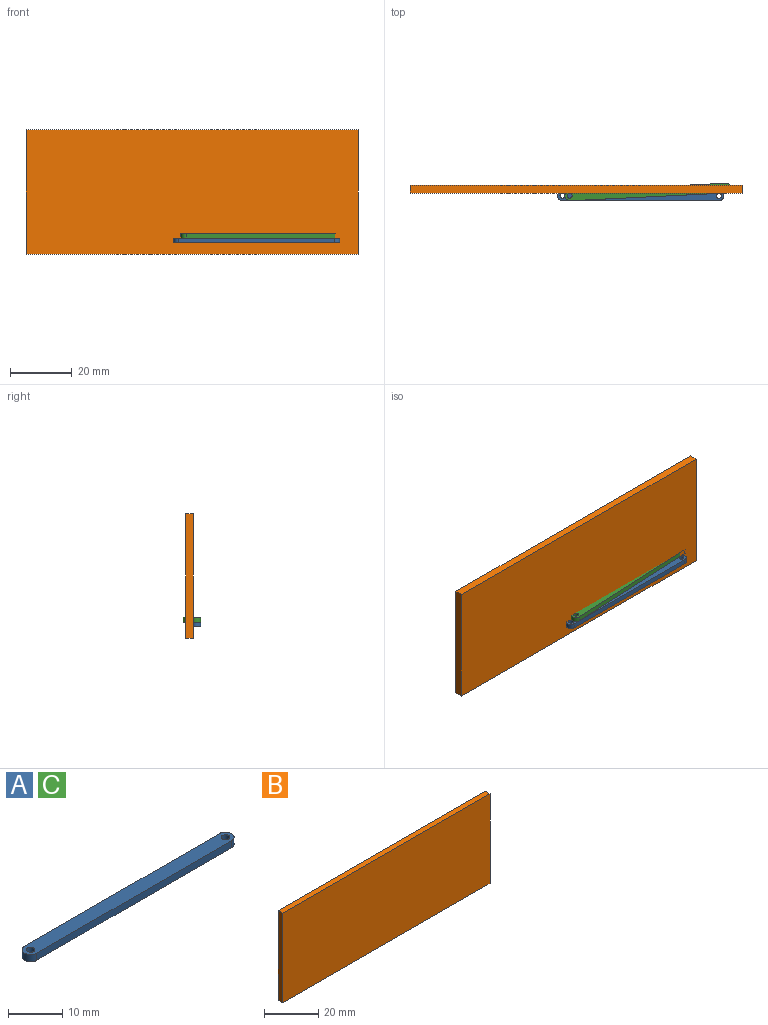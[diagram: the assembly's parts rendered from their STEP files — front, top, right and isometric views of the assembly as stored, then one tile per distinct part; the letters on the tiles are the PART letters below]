
ASSEMBLY  parts=3 mates=2
PART A: 8 faces, bbox 54x3.2x1.6 mm
  f0: plane 50.8x1.59mm, normal (0,1,0), area 80.6mm2, adj f1,f5,f6,f7
  f1: cylinder r=1.59mm len=3.18mm, axis (0,0,-1), area 7.9mm2, adj f0,f2,f6,f7
  f2: plane 50.8x1.59mm, normal (0,-1,0), area 80.6mm2, adj f1,f5,f6,f7
  f3: cylinder r=0.79mm len=1.59mm, axis (0,0,-1), area 7.9mm2, adj f6,f7
  f4: cylinder r=0.79mm len=1.59mm, axis (0,0,-1), area 7.9mm2, adj f6,f7
  f5: cylinder r=1.59mm len=3.18mm, axis (0,0,-1), area 7.9mm2, adj f0,f2,f6,f7
  f6: plane 53.98x3.18mm, normal (0,0,1), area 165.2mm2, adj f0,f1,f2,f3,f4,f5
  f7: plane 53.98x3.18mm, normal (0,0,-1), area 165.2mm2, adj f0,f1,f2,f3,f4,f5
PART B: 6 faces, bbox 107.8x2.5x40.4 mm
  f0: plane 107.81x2.54mm, normal (0,0,1), area 273.8mm2, adj f1,f3,f4,f5
  f1: plane 40.38x2.54mm, normal (-1,0,0), area 102.6mm2, adj f0,f2,f4,f5
  f2: plane 107.81x2.54mm, normal (0,0,-1), area 273.8mm2, adj f1,f3,f4,f5
  f3: plane 40.38x2.54mm, normal (1,0,0), area 102.6mm2, adj f0,f2,f4,f5
  f4: plane 107.81x40.38mm, normal (0,1,0), area 4353.3mm2, adj f0,f1,f2,f3
  f5: plane 107.81x40.38mm, normal (0,-1,0), area 4353.3mm2, adj f0,f1,f2,f3
PART C: same geometry as A
PLACE A t=(25.4,0,0)mm
PLACE B t=(-0.01,0.79,0)mm
PLACE C rot(axis=(0,0,1),2.8deg) t=(27.75,1.25,1.59)mm
MATE planar A.f6 <-> C.f7  axis (0,0,1) through (25.4,0,1.59)mm
MATE parallel A.f0 <-> B.f5  axis (0,1,0) through (25.4,1.59,0.79)mm
